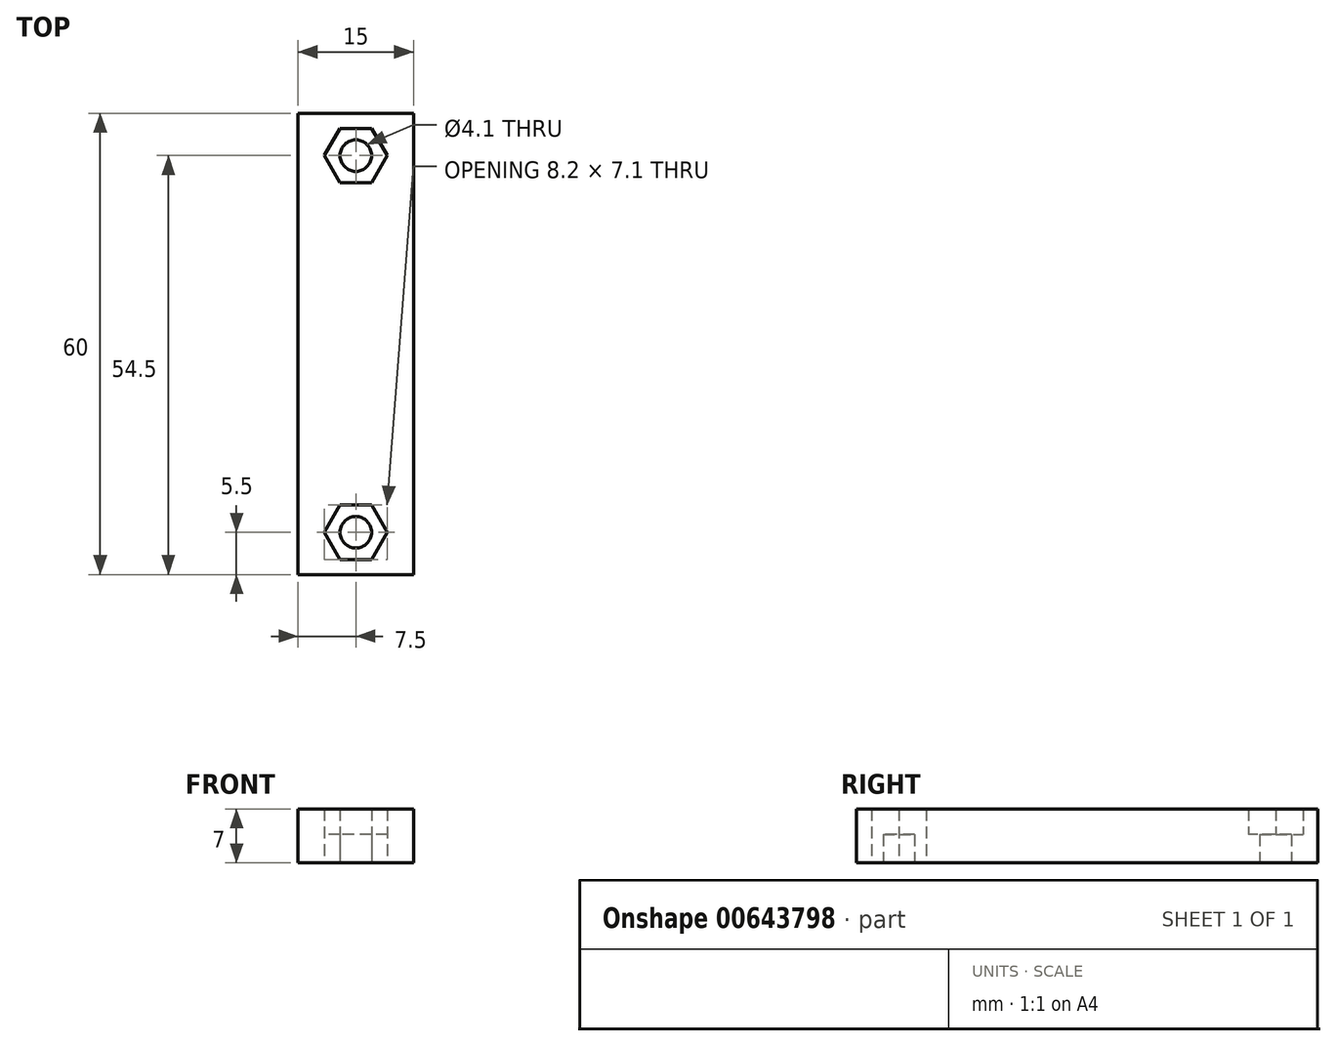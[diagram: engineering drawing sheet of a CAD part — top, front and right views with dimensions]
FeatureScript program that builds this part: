
annotation { "Feature Type Name" : "Feature", "Feature Type Description" : "" }
export const myFeature = defineFeature(function(context is Context, id is Id, definition is map)
    precondition{}
    {
        {
            var Q0;
            Q0=qCreatedBy(makeId("Top.planeOp"),FACE);
            var sketch = newSketch(context, id + "F0", { "sketchPlane" : qUnion([Q0])});
            skLineSegment(sketch, "E0.bottom", {"start": v(7.5, 30) * mm, "end": v(-7.5, 30) * mm});
            skLineSegment(sketch, "E0.top", {"start": v(7.5, -30) * mm, "end": v(-7.5, -30) * mm});
            skLineSegment(sketch, "E0.left", {"start": v(7.5, 30) * mm, "end": v(7.5, -30) * mm});
            skLineSegment(sketch, "E0.right", {"start": v(-7.5, 30) * mm, "end": v(-7.5, -30) * mm});
            skPoint(sketch, "E0.middle", {"position": v(0, 0) * mm});
            skCircle(sketch, "E1", {"center": v(0, 24.5) * mm, "radius": 2.05 * mm});
            skLineSegment(sketch, "E2.0", {"start": v(2.05, 20.95) * mm, "end": v(-2.05, 20.95) * mm});
            skLineSegment(sketch, "E2.1", {"start": v(-2.05, 20.95) * mm, "end": v(-4.1, 24.5) * mm});
            skLineSegment(sketch, "E2.2", {"start": v(-4.1, 24.5) * mm, "end": v(-2.05, 28.05) * mm});
            skLineSegment(sketch, "E2.3", {"start": v(-2.05, 28.05) * mm, "end": v(2.05, 28.05) * mm});
            skLineSegment(sketch, "E2.4", {"start": v(2.05, 28.05) * mm, "end": v(4.1, 24.5) * mm});
            skLineSegment(sketch, "E2.5", {"start": v(4.1, 24.5) * mm, "end": v(2.05, 20.95) * mm});
            skCircle(sketch, "E3.MirrorC", {"center": v(0, -24.5) * mm, "radius": 2.05 * mm});
            skLineSegment(sketch, "E4.MirrorCS", {"start": v(2.05, -20.95) * mm, "end": v(-2.05, -20.95) * mm});
            skLineSegment(sketch, "E5.MirrorCS", {"start": v(-2.05, -20.95) * mm, "end": v(-4.1, -24.5) * mm});
            skLineSegment(sketch, "E6.MirrorCS", {"start": v(-4.1, -24.5) * mm, "end": v(-2.05, -28.05) * mm});
            skLineSegment(sketch, "E7.MirrorCS", {"start": v(-2.05, -28.05) * mm, "end": v(2.05, -28.05) * mm});
            skLineSegment(sketch, "E8.MirrorCS", {"start": v(4.1, -24.5) * mm, "end": v(2.05, -20.95) * mm});
            skLineSegment(sketch, "E9.MirrorCS", {"start": v(2.05, -28.05) * mm, "end": v(4.1, -24.5) * mm});
            skSolve(sketch);
        }
        {
            var Q0;
            Q0 = qSketchRegion(id + "F0", true);
            extrude(context, id + "F1", {"entities" : qUnion([Q0]), "depth" : 7 * mm, "offsetDistance" : 25.4 * mm});
        }
        {
            var Q0;
            Q0=makeQuery(id+"F0.imprint","IMPRINT",FACE,{"disambiguationData":[TD([[makeQuery(id+"F0.imprint","IMPRINT",EDGE,{"derivedFrom":sQuery(id+"F0.wireOp",EDGE,"E3.MirrorC")}),1.0]])]});
            var Q1;
            Q1=makeQuery(id+"F0.imprint","IMPRINT",FACE,{"disambiguationData":[TD([[makeQuery(id+"F0.imprint","IMPRINT",EDGE,{"derivedFrom":sQuery(id+"F0.wireOp",EDGE,"E1")}),-1.0]])]});
            extrude(context, id + "F2", {"entities" : qUnion([Q0, Q1]), "operationType" : NewBodyOperationType.ADD, "depth" : 3.7 * mm, "offsetDistance" : 25.4 * mm});
        }
    });
